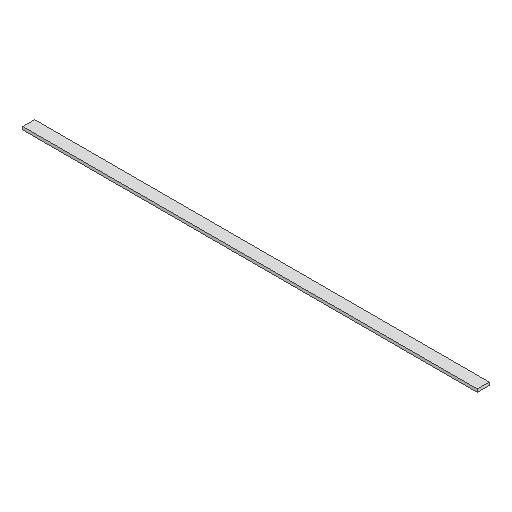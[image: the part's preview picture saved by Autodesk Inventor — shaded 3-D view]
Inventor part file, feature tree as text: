
AUTODESK INVENTOR PART (.ipt)
format: ipt  version: 2024 (Build 280153000, 153)  size: 79,872 bytes
history: native  units: mm
features: other x3, sketch x1
ambient origin geometry x8: Origin, YZ Plane, XZ Plane, XY Plane, X Axis, Y Axis, Z Axis, Center Point
bodies: Solid1 (feature_tree)
feature tree (4):
  other  "boxsectiontest.ipt"
  other  "Solid1::boxsectiontest.ipt"
  other  "TaggingFeature1"
  sketch  "Sketch1"  dims[d0=10.0mm]
